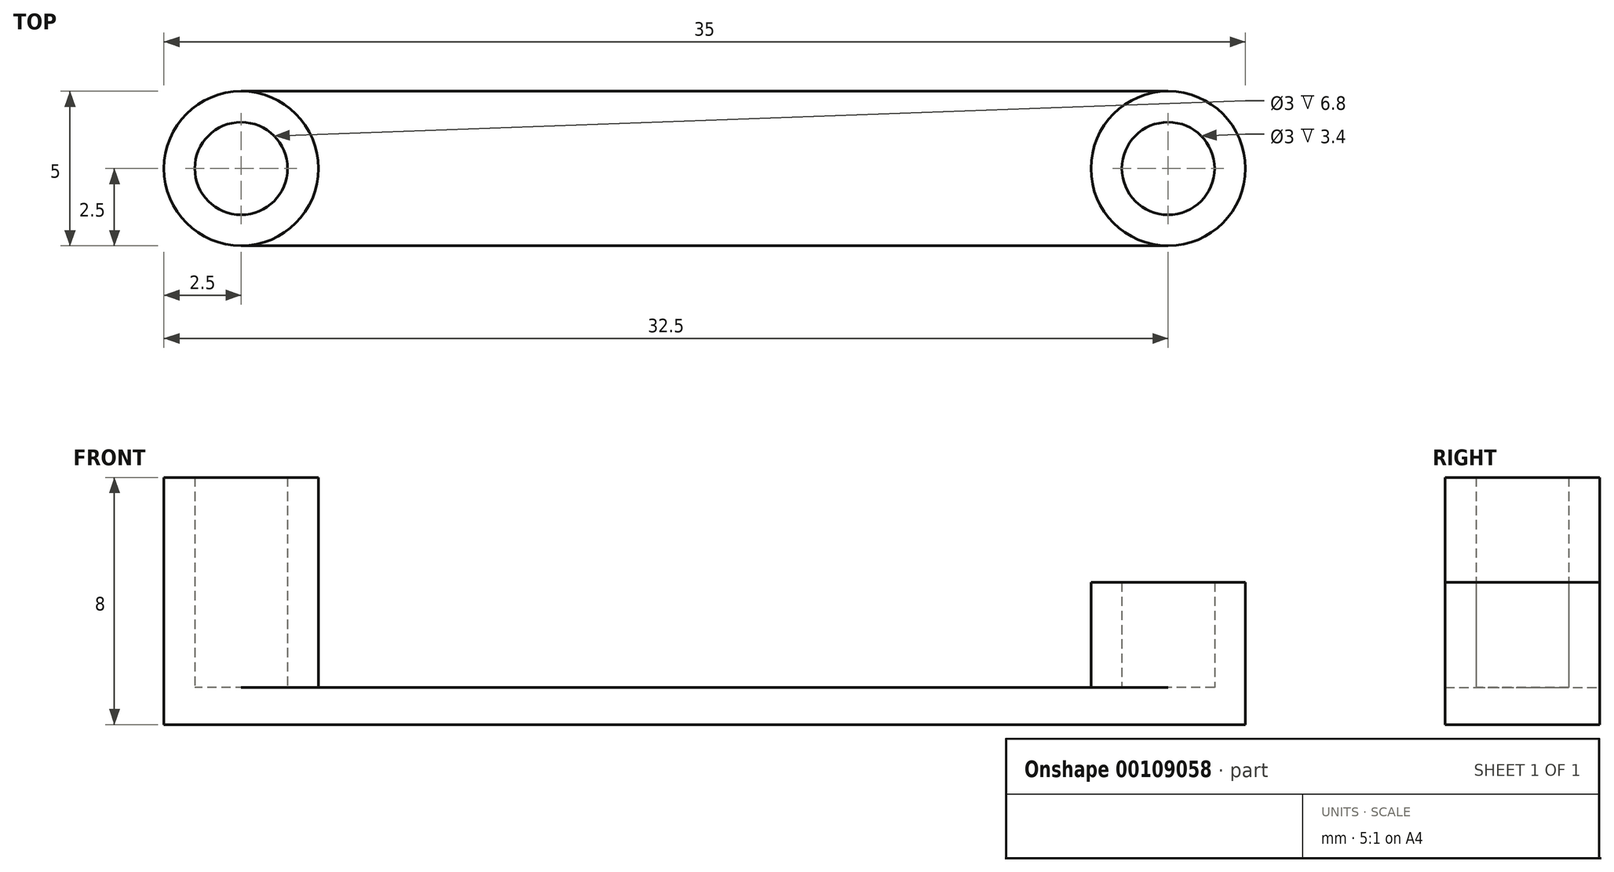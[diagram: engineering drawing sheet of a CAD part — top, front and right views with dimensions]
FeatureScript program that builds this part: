
annotation { "Feature Type Name" : "Feature", "Feature Type Description" : "" }
export const myFeature = defineFeature(function(context is Context, id is Id, definition is map)
    precondition{}
    {
        {
            var Q0;
            Q0=qCreatedBy(makeId("Top.planeOp"),FACE);
            var sketch = newSketch(context, id + "F0", { "sketchPlane" : qUnion([Q0])});
            skCircle(sketch, "E0", {"center": v(0, 0) * mm, "radius": 1.5 * mm});
            skCircle(sketch, "E1", {"center": v(0, 0) * mm, "radius": 2.5 * mm});
            skSolve(sketch);
        }
        {
            var Q0;
            Q0 = qSketchRegion(id + "F0", true);
            extrude(context, id + "F1", {"entities" : qUnion([Q0]), "depth" : 6.8 * mm});
        }
        {
            var Q0;
            Q0=makeQuery(id+"F1.opExtrude","CAP_FACE",FACE,{"disambiguationData":[OSD([sQuery(id+"F0.wireOp",EDGE,"E0"),sQuery(id+"F0.wireOp",EDGE,"E1")])],"isStart":true});
            var sketch = newSketch(context, id + "F2", { "sketchPlane" : qUnion([Q0])});
            skLineSegment(sketch, "E2", {"start": v(0, 2.5) * mm, "end": v(30, 2.5) * mm});
            skLineSegment(sketch, "E3", {"start": v(0, -2.5) * mm, "end": v(30, -2.5) * mm});
            skCircle(sketch, "E4", {"center": v(30, 0) * mm, "radius": 2.5 * mm});
            skSolve(sketch);
        }
        {
            var Q0;
            Q0 = qSketchRegion(id + "F2", true);
            var Q1;
            Q1=makeQuery(id+"F2.imprint","IMPRINT",FACE,{"disambiguationData":[TD([[makeQuery(id+"F2.imprint","IMPRINT",EDGE,{"derivedFrom":makeQuery(id+"F1.opExtrude","CAP_EDGE",EDGE,{"disambiguationData":[OSD([sQuery(id+"F0.wireOp",EDGE,"E0")])],"isStart":true})}),-1.0]])]});
            var Q2;
            Q2=makeQuery(id+"F2.imprint","IMPRINT",FACE,{"disambiguationData":[TD([[makeQuery(id+"F2.imprint","IMPRINT",EDGE,{"derivedFrom":makeQuery(id+"F1.opExtrude","CAP_EDGE",EDGE,{"disambiguationData":[OSD([sQuery(id+"F0.wireOp",EDGE,"E0")])],"isStart":true})}),1.0]])]});
            var Q3;
            {var subQ0=sQuery(id+"F2.wireOp",EDGE,"E2");Q3=makeQuery(id+"F2.imprint","IMPRINT",FACE,{"disambiguationData":[TD([[makeQuery(id+"F2.imprint","IMPRINT",EDGE,{"derivedFrom":subQ0}),-1.0]])]});}
            extrude(context, id + "F3", {"entities" : qUnion([Q0, Q1, Q2, Q3]), "operationType" : NewBodyOperationType.ADD, "depth" : 1.2 * mm});
        }
        {
            var Q0;
            {var subQ0=sQuery(id+"F2.wireOp",EDGE,"E4");var subQ1=sQuery(id+"F2.wireOp",EDGE,"E3");var subQ2=sQuery(id+"F2.wireOp",EDGE,"E2");var subQ3=sQuery(id+"F0.wireOp",EDGE,"E1");Q0=makeQuery(id+"F3.boolean.opBoolean","SPLIT",FACE,{"disambiguationData":[TD([makeQuery(id+"F1.opExtrude","SWEPT_FACE",FACE,{"disambiguationData":[OSD([subQ3])]})])],"derivedFrom":makeQuery(id+"F3.opExtrude","CAP_FACE",FACE,{"disambiguationData":[OSD([subQ3,subQ2,subQ1,subQ0])],"isStart":true})});}
            var sketch = newSketch(context, id + "F4", { "sketchPlane" : qUnion([Q0])});
            skCircle(sketch, "E5", {"center": v(30, 0) * mm, "radius": 1.5 * mm});
            skCircle(sketch, "E6", {"center": v(30, 0) * mm, "radius": 2.5 * mm});
            skSolve(sketch);
        }
        {
            var Q0;
            Q0=makeQuery(id+"F4.imprint","IMPRINT",FACE,{"disambiguationData":[TD([[makeQuery(id+"F4.imprint","IMPRINT",EDGE,{"derivedFrom":sQuery(id+"F4.wireOp",EDGE,"E5")}),-1.0]])]});
            extrude(context, id + "F5", {"entities" : qUnion([Q0]), "operationType" : NewBodyOperationType.ADD, "depth" : 3.4 * mm});
        }
    });
